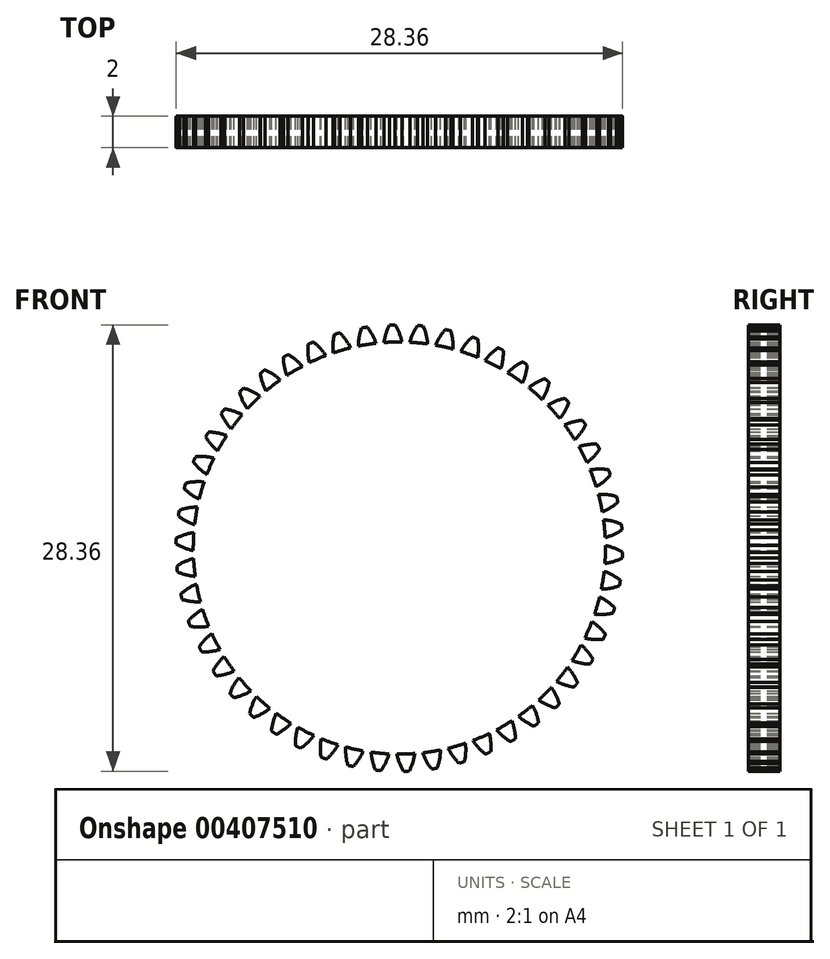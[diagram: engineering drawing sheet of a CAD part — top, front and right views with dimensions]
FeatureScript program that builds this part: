
annotation { "Feature Type Name" : "Feature", "Feature Type Description" : "" }
export const myFeature = defineFeature(function(context is Context, id is Id, definition is map)
    precondition{}
    {
        {
            var Q0;
            Q0=qCreatedBy(makeId("Front.planeOp"),FACE);
            var sketch = newSketch(context, id + "F0", { "sketchPlane" : qUnion([Q0])});
            skCircle(sketch, "E0", {"center": v(0, 0) * mm, "radius": 13.1 * mm});
            skCircle(sketch, "E1", {"center": v(0, 0) * mm, "radius": 13.63 * mm, "construction": true});
            skCircle(sketch, "E2", {"center": v(0, 0) * mm, "radius": 14.18 * mm, "construction": true});
            skLineSegment(sketch, "E3", {"start": v(0, 0) * mm, "end": v(0, 27.61) * mm, "construction": true});
            skLineSegment(sketch, "E4", {"start": v(0, 0) * mm, "end": v(-0.87, 27.82) * mm, "construction": true});
            skLineSegment(sketch, "E5", {"start": v(0, 13.63) * mm, "end": v(-5.77, 13.63) * mm, "construction": true});
            skLineSegment(sketch, "E6", {"start": v(0, 13.63) * mm, "end": v(-5.6, 11.6) * mm, "construction": true});
            skCircle(sketch, "E7", {"center": v(0, 0) * mm, "radius": 12.81 * mm, "construction": true});
            skCircle(sketch, "E8", {"center": v(0, 13.63) * mm, "radius": 3.41 * mm, "construction": true});
            skCircle(sketch, "E9", {"center": v(-3.18, 12.41) * mm, "radius": 3.41 * mm, "construction": true});
            skArc(sketch, "E10", {"start": v(0.16, 13.09) * mm, "mid": v(0, 13.65) * mm, "end": v(-0.26, 14.18) * mm});
            skArc(sketch, "E11.MirrorCS", {"start": v(-0.98, 13.05) * mm, "mid": v(-0.85, 13.62) * mm, "end": v(-0.63, 14.17) * mm});
            skArc(sketch, "E12", {"start": v(-0.26, 14.18) * mm, "mid": v(-0.45, 14.18) * mm, "end": v(-0.63, 14.17) * mm});
            skLineSegment(sketch, "E13", {"start": v(0.16, 13.09) * mm, "end": v(0.16, 13.09) * mm});
            skLineSegment(sketch, "E14", {"start": v(0.16, 13.09) * mm, "end": v(0.16, 13.08) * mm});
            skLineSegment(sketch, "E15", {"start": v(-0.98, 13.05) * mm, "end": v(-0.98, 13.05) * mm});
            skLineSegment(sketch, "E16", {"start": v(-0.98, 13.04) * mm, "end": v(-0.98, 13.05) * mm});
            skSolve(sketch);
        }
        {
            var Q0;
            {var subQ0=sQuery(id+"F0.wireOp",EDGE,"E10");Q0=makeQuery(id+"F0.imprint","IMPRINT",FACE,{"disambiguationData":[TD([[makeQuery(id+"F0.imprint","IMPRINT",EDGE,{"derivedFrom":subQ0}),1.0]])]});}
            var Q1;
            {var subQ0=sQuery(id+"F0.wireOp",EDGE,"E0");var subQ1=makeQuery(id+"F0.imprint","IMPRINT",VERTEX,{"disambiguationData":[OD(0.0)],"derivedFrom":subQ0});Q1=makeQuery(id+"F0.imprint","IMPRINT",FACE,{"disambiguationData":[TD([[makeQuery(id+"F0.imprint","IMPRINT",EDGE,{"disambiguationData":[TD([[subQ1,-1.0]])],"derivedFrom":subQ0}),1.0]])]});}
            extrude(context, id + "F1", {"entities" : qUnion([Q0, Q1]), "depth" : 2 * mm});
        }
        {
            var Q0;
            Q0=makeQuery(id+"F1.opExtrude","SWEPT_BODY",BODY,{"disambiguationData":[OSD([sQuery(id+"F0.wireOp",EDGE,"E0"),sQuery(id+"F0.wireOp",EDGE,"E10"),sQuery(id+"F0.wireOp",EDGE,"E11.MirrorCS"),sQuery(id+"F0.wireOp",EDGE,"E12")])]});
            var Q1;
            {var subQ0=sQuery(id+"F0.wireOp",EDGE,"E0");Q1=makeQuery(id+"F1.opExtrude","SWEPT_FACE",FACE,{"disambiguationData":[OSD([subQ0]),TDD([makeQuery(id+"F0.imprint","IMPRINT",EDGE,{"disambiguationData":[TD([[makeQuery(id+"F0.imprint","IMPRINT",VERTEX,{"disambiguationData":[OD(0.0)],"derivedFrom":subQ0}),1.0]])],"derivedFrom":subQ0})])]});}
            circularPattern(context, id + "F2", {"entities" : qUnion([Q0]), "axis" : qUnion([Q1]), "angle" : 360 * degree, "instanceCount" : 50, "equalSpace" : true});
        }
        {
            var Q0;
            Q0=makeQuery(id+"F2.opPattern","COPY",BODY,{"derivedFrom":makeQuery(id+"F1.opExtrude","SWEPT_BODY",BODY,{"disambiguationData":[OSD([sQuery(id+"F0.wireOp",EDGE,"E0"),sQuery(id+"F0.wireOp",EDGE,"E10"),sQuery(id+"F0.wireOp",EDGE,"E11.MirrorCS"),sQuery(id+"F0.wireOp",EDGE,"E12")])]}),"instanceName":"43"});
            transform(context, id + "F3", {"entities" : qUnion([Q0]), "transformType" : TransformType.TRANSLATION_3D, "dx" : 0 * mm, "dy" : 0 * mm, "dz" : 0 * mm, "makeCopy" : true});
        }
        {
            var Q0;
            Q0=makeQuery(id+"F3.opPattern","COPY",BODY,{"derivedFrom":makeQuery(id+"F2.opPattern","COPY",BODY,{"derivedFrom":makeQuery(id+"F1.opExtrude","SWEPT_BODY",BODY,{"disambiguationData":[OSD([sQuery(id+"F0.wireOp",EDGE,"E0"),sQuery(id+"F0.wireOp",EDGE,"E10"),sQuery(id+"F0.wireOp",EDGE,"E11.MirrorCS"),sQuery(id+"F0.wireOp",EDGE,"E12")])]}),"instanceName":"43"}),"instanceName":"1"});
            deleteBodies(context, id + "F4", {"entities" : qUnion([Q0])});
        }
    });
